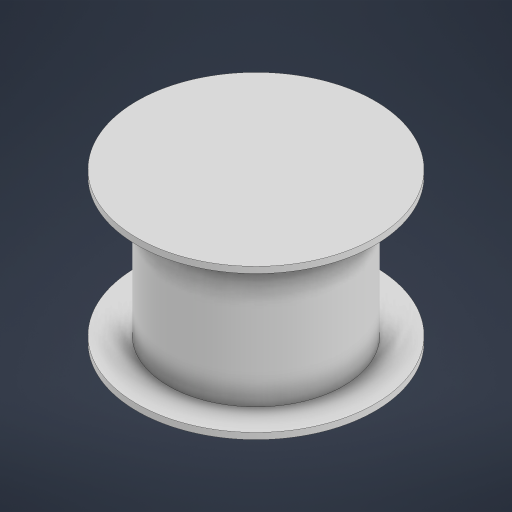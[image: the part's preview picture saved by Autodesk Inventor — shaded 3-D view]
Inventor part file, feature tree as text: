
AUTODESK INVENTOR PART (.ipt)
format: ipt  version: 2023 (Build 270158030, 158C)  size: 192,000 bytes
history: native  units: in
note: dims shown in document units (in); Inventor stores cm internally (conversion verified against a paired STEP export)
features: extrude x3, sketch x3
ambient origin geometry x8: Origin, YZ Plane, XZ Plane, XY Plane, X Axis, Y Axis, Z Axis, Center Point
bodies: Solid1 (feature_tree)
feature tree (6):
  extrude  "Extrusion1"  Depth=0.9449in
  sketch  "Sketch3"  dims[d4=0.0394in d5=0.0in d7=1.1024in]
  extrude  "Extrusion3"  Depth=0.0394in
  sketch  "Sketch5"  dims[d10=0.8661in d11=0.0in d14=0.0394in d15=0.0in]
  extrude  "Extrusion5"  Depth=0.0394in TaperAngle=0.0deg
  sketch  "Sketch1"  dims[d1=1.4961in d3=0.9449in]
